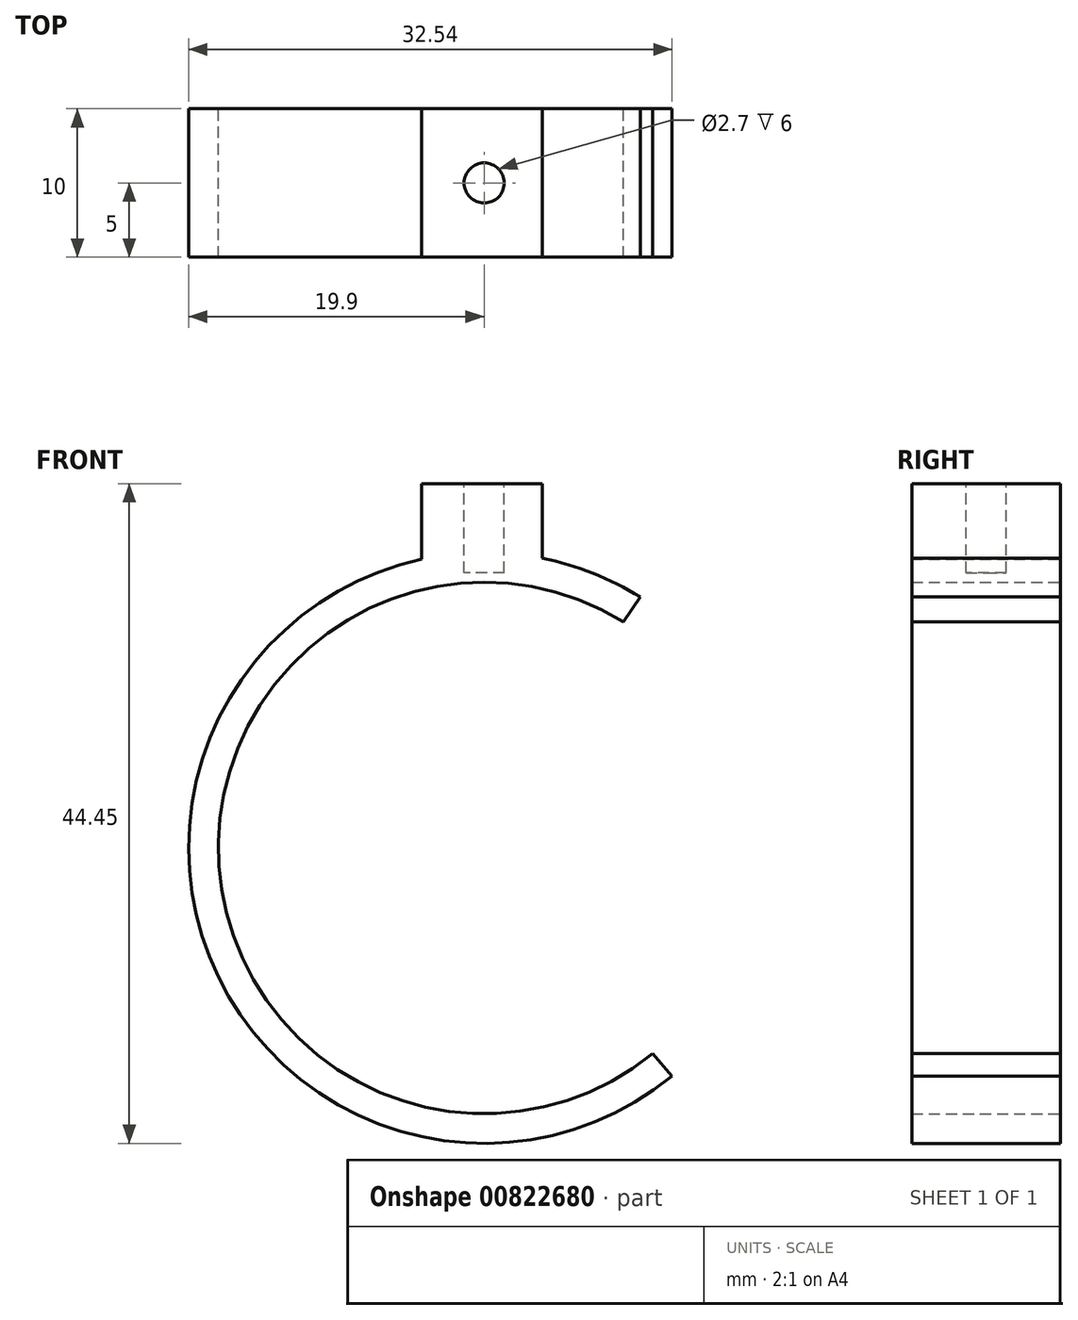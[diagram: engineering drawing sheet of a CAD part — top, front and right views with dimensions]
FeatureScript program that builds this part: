
annotation { "Feature Type Name" : "Feature", "Feature Type Description" : "" }
export const myFeature = defineFeature(function(context is Context, id is Id, definition is map)
    precondition{}
    {
        {
            var Q0;
            Q0=qCreatedBy(makeId("Front.planeOp"),FACE);
            var sketch = newSketch(context, id + "F0", { "sketchPlane" : qUnion([Q0])});
            skArc(sketch, "E0", {"start": v(9.38, 15.25) * mm, "mid": v(-17.86, -1.2) * mm, "end": v(11.35, -13.84) * mm});
            skArc(sketch, "E1", {"start": v(-4.2, 19.45) * mm, "mid": v(-17.92, -8.66) * mm, "end": v(12.64, -15.37) * mm});
            skLineSegment(sketch, "E2", {"start": v(9.38, 15.25) * mm, "end": v(10.5, 16.9) * mm});
            skLineSegment(sketch, "E3", {"start": v(11.35, -13.84) * mm, "end": v(12.64, -15.37) * mm});
            skLineSegment(sketch, "E4", {"start": v(-4.2, 19.45) * mm, "end": v(-4.2, 24.55) * mm});
            skLineSegment(sketch, "E5", {"start": v(-4.2, 24.55) * mm, "end": v(3.92, 24.55) * mm});
            skLineSegment(sketch, "E6", {"start": v(3.92, 24.55) * mm, "end": v(3.92, 19.45) * mm});
            skArc(sketch, "E7.trimOffspring", {"start": v(10.5, 16.9) * mm, "mid": v(7.33, 18.5) * mm, "end": v(3.92, 19.51) * mm});
            skSolve(sketch);
        }
        {
            var Q0;
            Q0=makeQuery(id+"F0.imprint","IMPRINT",FACE,{"disambiguationData":[TD([[makeQuery(id+"F0.imprint","IMPRINT",EDGE,{"derivedFrom":sQuery(id+"F0.wireOp",EDGE,"E0")}),-1.0]])]});
            extrude(context, id + "F1", {"entities" : qUnion([Q0]), "depth" : 10 * mm, "offsetDistance" : 25 * mm});
        }
        {
            var Q0;
            Q0=makeQuery(id+"F1.opExtrude","SWEPT_FACE",FACE,{"disambiguationData":[OSD([sQuery(id+"F0.wireOp",EDGE,"E5")])]});
            var sketch = newSketch(context, id + "F2", { "sketchPlane" : qUnion([Q0])});
            skCircle(sketch, "E8", {"center": v(0, -5) * mm, "radius": 1.35 * mm});
            skPoint(sketch, "E8.centerSnap0", {"position": v(3.92, -5) * mm});
            skSolve(sketch);
        }
        {
            var Q0;
            Q0=makeQuery(id+"F2.imprint","IMPRINT",FACE,{"disambiguationData":[TD([[makeQuery(id+"F2.imprint","IMPRINT",EDGE,{"derivedFrom":sQuery(id+"F2.wireOp",EDGE,"E8")}),1.0]])]});
            extrude(context, id + "F3", {"entities" : qUnion([Q0]), "operationType" : NewBodyOperationType.REMOVE, "oppositeDirection" : true, "depth" : (6) * mm, "offsetDistance" : 25 * mm});
        }
    });
